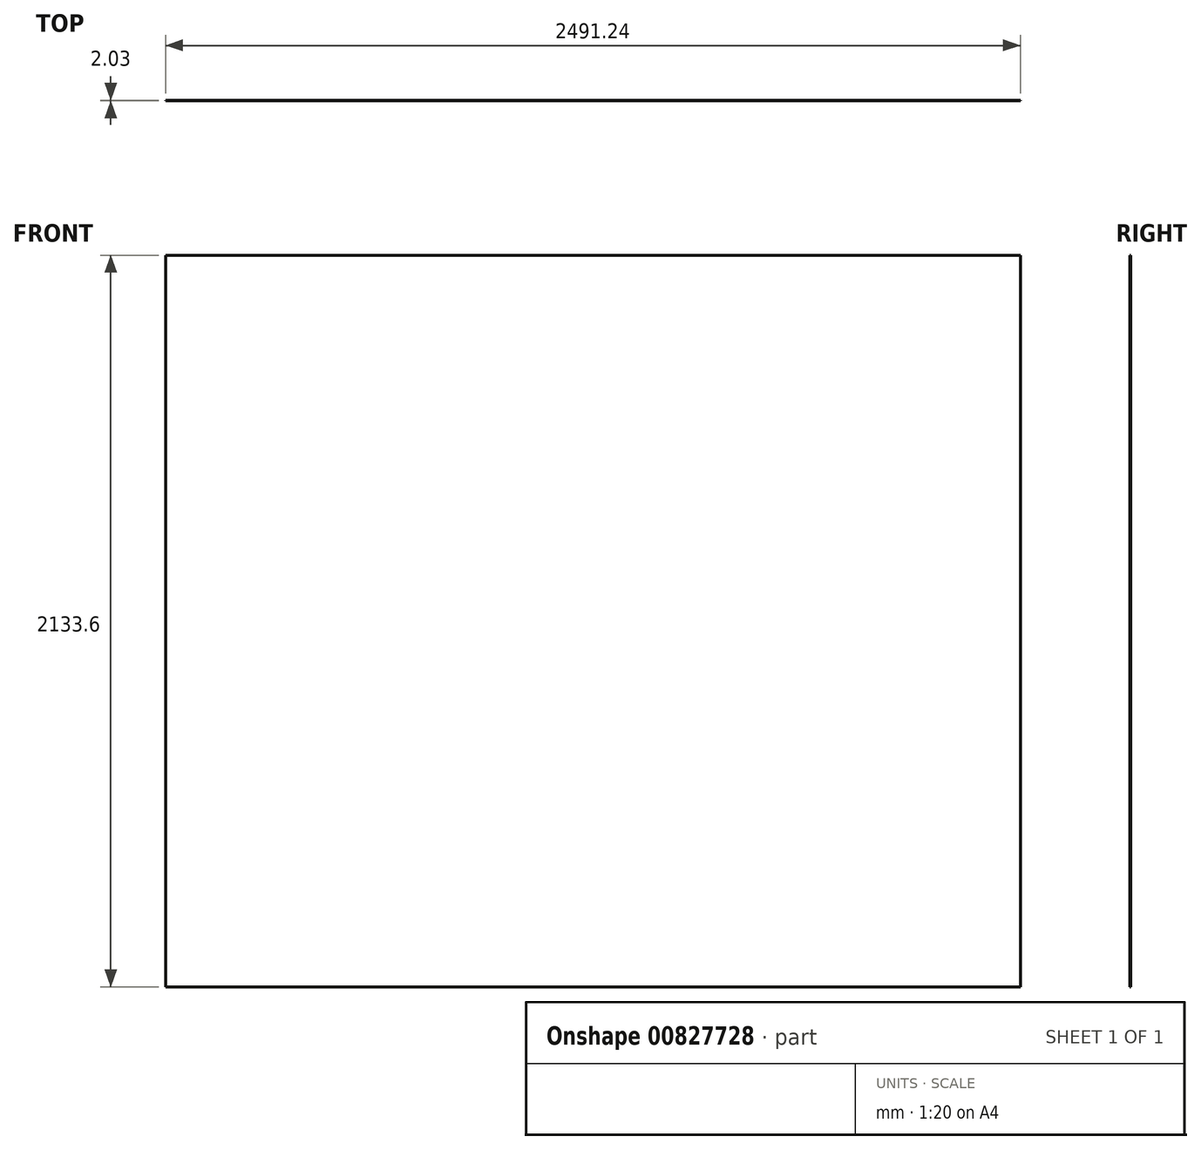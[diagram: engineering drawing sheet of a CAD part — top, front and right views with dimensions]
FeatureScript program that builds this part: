
annotation { "Feature Type Name" : "Feature", "Feature Type Description" : "" }
export const myFeature = defineFeature(function(context is Context, id is Id, definition is map)
    precondition{}
    {
        {
            var Q0;
            Q0=qCreatedBy(makeId("Front.planeOp"),FACE);
            var sketch = newSketch(context, id + "F0", { "sketchPlane" : qUnion([Q0])});
            skLineSegment(sketch, "E0.bottom", {"start": v(-2409.49, 314.8) * mm, "end": v(81.75, 314.8) * mm});
            skLineSegment(sketch, "E0.top", {"start": v(-2409.49, -1818.8) * mm, "end": v(81.75, -1818.8) * mm});
            skLineSegment(sketch, "E0.left", {"start": v(-2409.49, 314.8) * mm, "end": v(-2409.49, -1818.8) * mm});
            skLineSegment(sketch, "E0.right", {"start": v(81.75, 314.8) * mm, "end": v(81.75, -1818.8) * mm});
            skSolve(sketch);
        }
        {
            var Q0;
            Q0=qSketchRegion(id+"F0",true);
            extrude(context, id + "F1", {"entities" : qUnion([Q0]), "depth" : 2.03 * mm, "offsetDistance" : 25.4 * mm});
        }
    });
